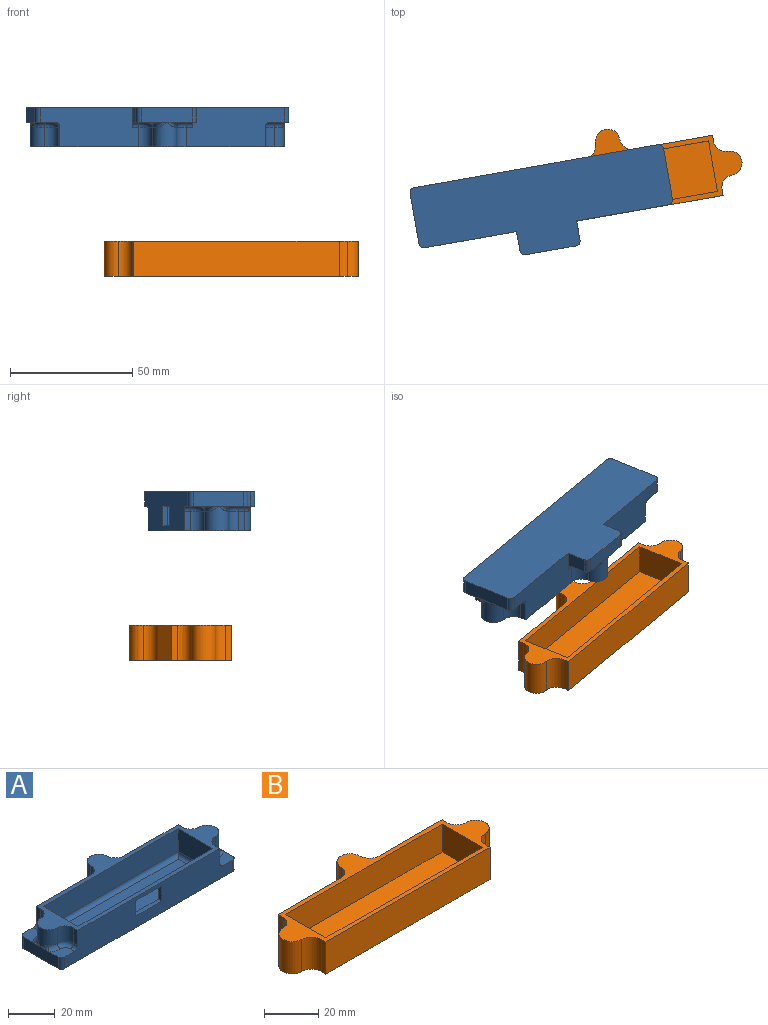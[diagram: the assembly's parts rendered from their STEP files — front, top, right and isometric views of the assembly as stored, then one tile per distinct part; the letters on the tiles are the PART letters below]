
ASSEMBLY  parts=2 mates=1
PART A: 72 faces, bbox 108.5x35.4x16 mm
  f0: plane 40.75x16mm, normal (0,1,0), area 552.9mm2, adj f1,f4,f12,f24,f38,f46,f47,f51
  f1: plane 8x2.5mm, normal (1,0,0), area 20mm2, adj f0,f12,f28,f51
  f2: plane 8x2.5mm, normal (-1,0,0), area 20mm2, adj f3,f12,f25,f59
  f3: plane 40.75x16mm, normal (0,1,0), area 552.9mm2, adj f2,f4,f12,f23,f31,f33,f40,f55
  f4: plane 105.5x35mm, normal (0,0,-1), area 2882.3mm2, adj f0,f3,f11,f31,f32,f34,f36,f37
  f5: plane 81.5x12mm, normal (0,-1,0), area 978mm2, adj f6,f8,f12,f14
  f6: plane 21x12mm, normal (1,0,0), area 252mm2, adj f5,f7,f12,f15
  f7: plane 81.5x12mm, normal (0,1,0), area 853.2mm2, adj f6,f8,f12,f17,f18,f19,f20,f21
  f8: plane 21x12mm, normal (-1,0,0), area 252mm2, adj f5,f7,f12,f16
  f9: plane 8x2.5mm, normal (-1,0,0), area 20mm2, adj f11,f12,f27,f71
  f10: plane 8x2.5mm, normal (1,0,0), area 20mm2, adj f11,f12,f30,f63
  f11: plane 101.5x16mm, normal (0,-1,0), area 1340.9mm2, adj f4,f9,f10,f12,f18,f19,f20,f21
  f12: plane 105.5x35mm, normal (0,0,1), area 726mm2, adj f0,f1,f2,f3,f5,f6,f7,f8
  f13: plane 77.5x17mm, normal (0,0,1), area 1317.5mm2, adj f14,f15,f16,f17
  f14: cylinder r=2mm len=81.5mm, axis (1,0,0), area 251.5mm2, adj f5,f13,f15,f16
  f15: cylinder r=2mm len=21mm, axis (0,1,0), area 61.4mm2, adj f6,f13,f14,f17
  f16: cylinder r=2mm len=21mm, axis (0,-1,0), area 61.4mm2, adj f8,f13,f14,f17
  f17: cylinder r=2mm len=81.5mm, axis (-1,0,0), area 251.5mm2, adj f7,f13,f15,f16
  f18: plane 8x2mm, normal (1,0,0), area 16mm2, adj f7,f11,f19,f21
  f19: plane 15.6x2mm, normal (0,0,1), area 31.2mm2, adj f7,f11,f18,f20
  f20: plane 8x2mm, normal (-1,0,0), area 16mm2, adj f7,f11,f19,f21
  f21: plane 15.6x2mm, normal (0,0,-1), area 31.2mm2, adj f7,f11,f18,f20
  f22: cylinder r=5mm len=10mm, axis (0,0,1), area 131.6mm2, adj f12,f23,f24,f52,f53,f66,f67
  f23: cylinder r=5mm len=8mm, axis (0,0,1), area 62.8mm2, adj f3,f12,f22,f54
  f24: cylinder r=5mm len=8mm, axis (0,0,1), area 62.8mm2, adj f0,f12,f22,f65
  f25: cylinder r=5mm len=8mm, axis (0,0,1), area 62.8mm2, adj f2,f12,f26,f58
  f26: cylinder r=5mm len=10mm, axis (0,0,1), area 131.6mm2, adj f12,f25,f27,f56,f57,f68,f69
  f27: cylinder r=5mm len=8mm, axis (0,0,1), area 62.8mm2, adj f9,f12,f26,f70
  f28: cylinder r=5mm len=8mm, axis (0,0,1), area 62.8mm2, adj f1,f12,f29,f50
  f29: cylinder r=5mm len=10mm, axis (0,0,1), area 131.6mm2, adj f12,f28,f30,f48,f49,f60,f61
  f30: cylinder r=5mm len=8mm, axis (0,0,1), area 62.8mm2, adj f10,f12,f29,f62
  f31: cylinder r=2mm len=6mm, axis (0,0,-1), area 18.8mm2, adj f3,f4,f32,f33
  f32: plane 21x6mm, normal (-1,0,0), area 126mm2, adj f4,f31,f33,f34,f35,f56,f68
  f33: plane 8x7.6mm, normal (0,0,1), area 44.5mm2, adj f3,f31,f32,f57,f58,f59
  f34: cylinder r=2mm len=6mm, axis (0,0,-1), area 18.8mm2, adj f4,f11,f32,f35
  f35: plane 8x7.6mm, normal (0,0,1), area 44.5mm2, adj f11,f32,f34,f69,f70,f71
  f36: plane 21x6mm, normal (0,1,0), area 126mm2, adj f4,f37,f39,f41,f42,f52,f67
  f37: cylinder r=2mm len=6mm, axis (0,0,-1), area 18.8mm2, adj f4,f36,f38,f39
  f38: plane 8x8mm, normal (1,0,0), area 48.9mm2, adj f0,f4,f37,f39,f64
  f39: plane 8x7.6mm, normal (0,0,1), area 44.5mm2, adj f36,f37,f38,f64,f65,f66
  f40: plane 8x8mm, normal (-1,0,0), area 48.9mm2, adj f3,f4,f41,f42,f55
  f41: cylinder r=2mm len=6mm, axis (0,0,-1), area 18.8mm2, adj f4,f36,f40,f42
  f42: plane 8x7.6mm, normal (0,0,1), area 44.5mm2, adj f36,f40,f41,f53,f54,f55
  f43: cylinder r=2mm len=6mm, axis (0,0,-1), area 18.8mm2, adj f4,f11,f44,f45
  f44: plane 21x6mm, normal (1,0,0), area 126mm2, adj f4,f43,f45,f46,f47,f48,f60
  f45: plane 8x7.6mm, normal (0,0,1), area 44.5mm2, adj f11,f43,f44,f61,f62,f63
  f46: cylinder r=2mm len=6mm, axis (0,0,-1), area 18.8mm2, adj f0,f4,f44,f47
  f47: plane 8x7.6mm, normal (0,0,1), area 44.5mm2, adj f0,f44,f46,f49,f50,f51
  f48: bspline ~5.05x2.1mm, area 6.1mm2, adj f29,f44,f49
  f49: torus R=7mm, axis (0,0,-1), area 14.3mm2, adj f29,f47,f48,f50
  f50: torus R=3mm, axis (0,0,-1), area 21.1mm2, adj f28,f47,f49,f51
  f51: cylinder r=2mm len=2.5mm, axis (0,-1,0), area 7.9mm2, adj f0,f1,f47,f50
  f52: bspline ~5.05x2.1mm, area 6.1mm2, adj f22,f36,f53
  f53: torus R=7mm, axis (0,0,-1), area 14.3mm2, adj f22,f42,f52,f54
  f54: torus R=3mm, axis (0,0,-1), area 21.1mm2, adj f23,f42,f53,f55
  f55: cylinder r=2mm len=2.5mm, axis (1,0,0), area 7.9mm2, adj f3,f40,f42,f54
  f56: bspline ~5.05x2.1mm, area 6.1mm2, adj f26,f32,f57
  f57: torus R=7mm, axis (0,0,-1), area 14.3mm2, adj f26,f33,f56,f58
  f58: torus R=3mm, axis (0,0,-1), area 21.1mm2, adj f25,f33,f57,f59
  f59: cylinder r=2mm len=2.5mm, axis (0,1,0), area 7.9mm2, adj f2,f3,f33,f58
  f60: bspline ~5.05x2.1mm, area 6.1mm2, adj f29,f44,f61
  f61: torus R=7mm, axis (0,0,-1), area 14.3mm2, adj f29,f45,f60,f62
  f62: torus R=3mm, axis (0,0,-1), area 21.1mm2, adj f30,f45,f61,f63
  f63: cylinder r=2mm len=2.5mm, axis (0,-1,0), area 7.9mm2, adj f10,f11,f45,f62
  f64: cylinder r=2mm len=2.5mm, axis (1,0,0), area 7.9mm2, adj f0,f38,f39,f65
  f65: torus R=3mm, axis (0,0,-1), area 21.1mm2, adj f24,f39,f64,f66
  f66: torus R=7mm, axis (0,0,-1), area 14.3mm2, adj f22,f39,f65,f67
  f67: bspline ~5.05x2.1mm, area 6.1mm2, adj f22,f36,f66
  f68: bspline ~5.05x2.1mm, area 6.1mm2, adj f26,f32,f69
  f69: torus R=7mm, axis (0,0,-1), area 14.3mm2, adj f26,f35,f68,f70
  f70: torus R=3mm, axis (0,0,-1), area 21.1mm2, adj f27,f35,f69,f71
  f71: cylinder r=2mm len=2.5mm, axis (0,1,0), area 7.9mm2, adj f9,f11,f35,f70
PART B: 23 faces, bbox 105.5x35x14.5 mm
  f0: plane 14.5x2.5mm, normal (1,0,0), area 36.3mm2, adj f4,f7,f12,f20
  f1: plane 14.5x2.5mm, normal (-1,0,0), area 36.3mm2, adj f5,f7,f12,f18
  f2: plane 14.5x2.5mm, normal (-1,0,0), area 36.3mm2, adj f3,f7,f12,f19
  f3: plane 32.75x14.5mm, normal (0,1,0), area 474.9mm2, adj f2,f7,f12,f15
  f4: plane 32.75x14.5mm, normal (0,1,0), area 474.9mm2, adj f0,f7,f12,f16
  f5: plane 85.5x14.5mm, normal (0,-1,0), area 1239.8mm2, adj f1,f6,f7,f12
  f6: plane 14.5x2.5mm, normal (1,0,0), area 36.3mm2, adj f5,f7,f12,f21
  f7: plane 105.5x35mm, normal (0,0,-1), area 2437.5mm2, adj f0,f1,f2,f3,f4,f5,f6,f14
  f8: plane 21x12.5mm, normal (1,0,0), area 262.5mm2, adj f9,f11,f12,f13
  f9: plane 81.5x12.5mm, normal (0,-1,0), area 1018.8mm2, adj f8,f10,f12,f13
  f10: plane 21x12.5mm, normal (-1,0,0), area 262.5mm2, adj f9,f11,f12,f13
  f11: plane 81.5x12.5mm, normal (0,1,0), area 1018.8mm2, adj f8,f10,f12,f13
  f12: plane 105.5x35mm, normal (0,0,1), area 726mm2, adj f0,f1,f2,f3,f4,f5,f6,f8
  f13: plane 81.5x21mm, normal (0,0,1), area 1711.5mm2, adj f8,f9,f10,f11
  f14: cylinder r=5mm len=14.5mm, axis (0,0,1), area 227.8mm2, adj f7,f12,f15,f16
  f15: cylinder r=5mm len=14.5mm, axis (0,0,1), area 113.9mm2, adj f3,f7,f12,f14
  f16: cylinder r=5mm len=14.5mm, axis (0,0,1), area 113.9mm2, adj f4,f7,f12,f14
  f17: cylinder r=5mm len=14.5mm, axis (0,0,1), area 227.8mm2, adj f7,f12,f18,f19
  f18: cylinder r=5mm len=14.5mm, axis (0,0,1), area 113.9mm2, adj f1,f7,f12,f17
  f19: cylinder r=5mm len=14.5mm, axis (0,0,1), area 113.9mm2, adj f2,f7,f12,f17
  f20: cylinder r=5mm len=14.5mm, axis (0,0,1), area 113.9mm2, adj f0,f7,f12,f22
  f21: cylinder r=5mm len=14.5mm, axis (0,0,1), area 113.9mm2, adj f6,f7,f12,f22
  f22: cylinder r=5mm len=14.5mm, axis (0,0,1), area 227.8mm2, adj f7,f12,f20,f21
PLACE A rot(axis=(1,0.09,0),180deg) t=(-8.31,23.89,87.6)mm
PLACE B rot(axis=(0,0,1),10deg) t=(15.96,51.53,18.42)mm
MATE planar A.f11 <-> B.f3  axis (-0.17,0.98,0) through (27.83,53.62,80.15)mm
